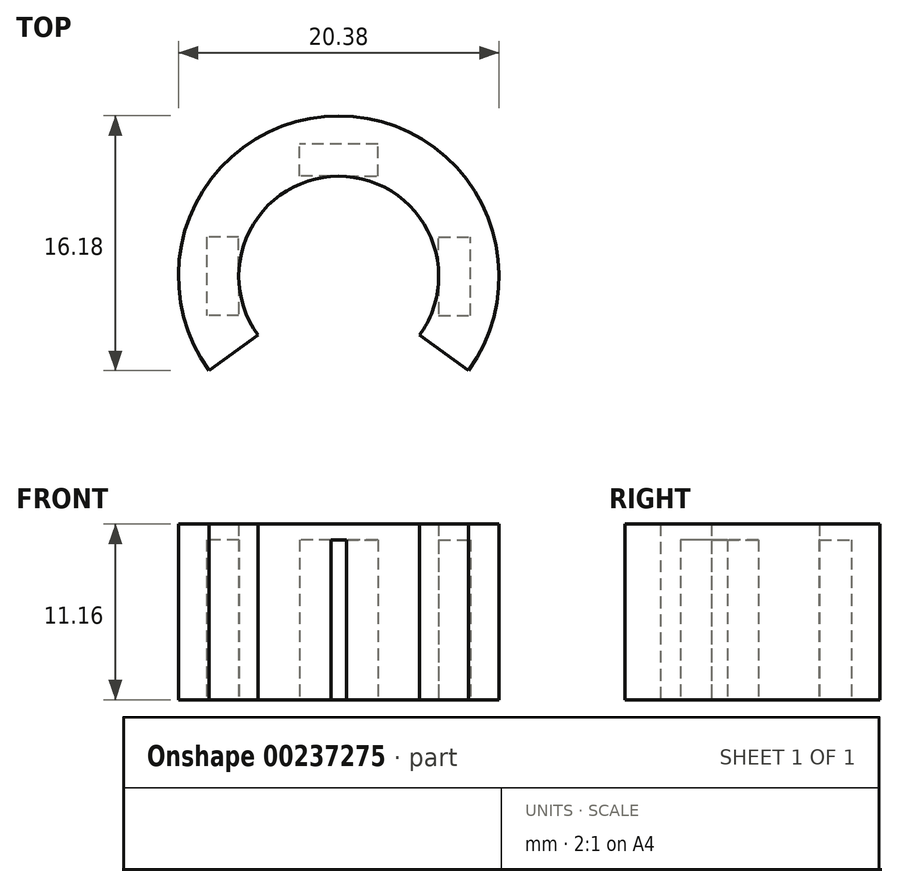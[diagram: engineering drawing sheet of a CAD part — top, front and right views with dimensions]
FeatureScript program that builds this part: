
annotation { "Feature Type Name" : "Feature", "Feature Type Description" : "" }
export const myFeature = defineFeature(function(context is Context, id is Id, definition is map)
    precondition{}
    {
        {
            var Q0;
            Q0=qCreatedBy(makeId("Top.planeOp"),FACE);
            var sketch = newSketch(context, id + "F0", { "sketchPlane" : qUnion([Q0])});
            skLineSegment(sketch, "E0.0", {"start": v(2.49, 6.35) * mm, "end": v(2.49, 8.38) * mm});
            skLineSegment(sketch, "E1.0", {"start": v(-2.49, 6.35) * mm, "end": v(-2.49, 8.38) * mm});
            skLineSegment(sketch, "E2", {"start": v(0.5, 6.35) * mm, "end": v(2.49, 6.35) * mm});
            skLineSegment(sketch, "E3", {"start": v(-0.5, 6.35) * mm, "end": v(-2.49, 6.35) * mm});
            skLineSegment(sketch, "E4.0", {"start": v(2.49, 8.38) * mm, "end": v(-2.49, 8.38) * mm});
            skLineSegment(sketch, "E5.0", {"start": v(3.99, 6.76) * mm, "end": v(3.99, 9.88) * mm});
            skArc(sketch, "E5.1", {"start": v(-3.99, 6.76) * mm, "mid": v(-5.55, 5.55) * mm, "end": v(-6.76, 3.99) * mm});
            skLineSegment(sketch, "E5.2", {"start": v(-3.99, 6.76) * mm, "end": v(-3.99, 9.88) * mm});
            skLineSegment(sketch, "E5.3", {"start": v(3.99, 9.88) * mm, "end": v(-3.99, 9.88) * mm});
            skArc(sketch, "E6.converted", {"start": v(-0.5, 6.33) * mm, "mid": v(-4.5, 4.5) * mm, "end": v(-6.33, 0.5) * mm});
            skPoint(sketch, "E7.orphan", {"position": v(-2.49, 5.84) * mm});
            skPoint(sketch, "E8.orphan", {"position": v(2.49, 5.84) * mm});
            skArc(sketch, "E9", {"start": v(-0.5, 6.35) * mm, "mid": v(-0.5, 6.34) * mm, "end": v(-0.5, 6.33) * mm});
            skArc(sketch, "E10.trimOffspring", {"start": v(0.5, 6.33) * mm, "mid": v(0.5, 6.34) * mm, "end": v(0.5, 6.35) * mm});
            skLineSegment(sketch, "E11.1.0", {"start": v(-9.88, 3.99) * mm, "end": v(-9.88, -3.99) * mm});
            skLineSegment(sketch, "E11.1.1", {"start": v(-6.76, -3.99) * mm, "end": v(-9.88, -3.99) * mm});
            skLineSegment(sketch, "E11.1.2", {"start": v(-6.76, 3.99) * mm, "end": v(-9.88, 3.99) * mm});
            skLineSegment(sketch, "E11.1.3", {"start": v(-8.38, 2.49) * mm, "end": v(-8.38, -2.49) * mm});
            skLineSegment(sketch, "E11.1.4", {"start": v(-6.35, -2.49) * mm, "end": v(-8.38, -2.49) * mm});
            skLineSegment(sketch, "E11.1.5", {"start": v(-6.35, 2.49) * mm, "end": v(-8.38, 2.49) * mm});
            skLineSegment(sketch, "E11.1.6", {"start": v(-6.35, 0.5) * mm, "end": v(-6.35, 2.49) * mm});
            skLineSegment(sketch, "E11.1.7", {"start": v(-6.35, -0.5) * mm, "end": v(-6.35, -2.49) * mm});
            skArc(sketch, "E11.1.9", {"start": v(-6.35, -0.5) * mm, "mid": v(-6.34, -0.5) * mm, "end": v(-6.33, -0.5) * mm});
            skArc(sketch, "E11.1.10", {"start": v(-6.33, 0.5) * mm, "mid": v(-6.34, 0.5) * mm, "end": v(-6.35, 0.5) * mm});
            skLineSegment(sketch, "E12.2.3.0", {"start": v(9.88, -3.99) * mm, "end": v(9.88, 3.99) * mm});
            skLineSegment(sketch, "E12.3.3.0", {"start": v(6.76, 3.99) * mm, "end": v(9.88, 3.99) * mm});
            skLineSegment(sketch, "E12.6.3.0", {"start": v(6.76, -3.99) * mm, "end": v(9.88, -3.99) * mm});
            skLineSegment(sketch, "E12.9.3.0", {"start": v(8.38, -2.49) * mm, "end": v(8.38, 2.49) * mm});
            skLineSegment(sketch, "E12.12.3.0", {"start": v(6.35, 2.49) * mm, "end": v(8.38, 2.49) * mm});
            skLineSegment(sketch, "E12.15.3.0", {"start": v(6.35, -2.49) * mm, "end": v(8.38, -2.49) * mm});
            skLineSegment(sketch, "E12.18.3.0", {"start": v(6.35, -0.5) * mm, "end": v(6.35, -2.49) * mm});
            skLineSegment(sketch, "E12.21.3.0", {"start": v(6.35, 0.5) * mm, "end": v(6.35, 2.49) * mm});
            skArc(sketch, "E12.28.3.0", {"start": v(6.35, 0.5) * mm, "mid": v(6.34, 0.5) * mm, "end": v(6.33, 0.5) * mm});
            skArc(sketch, "E12.32.3.0", {"start": v(6.33, -0.5) * mm, "mid": v(6.34, -0.5) * mm, "end": v(6.35, -0.5) * mm});
            skArc(sketch, "E13.trimOffspring", {"start": v(6.33, 0.5) * mm, "mid": v(4.5, 4.5) * mm, "end": v(0.5, 6.33) * mm});
            skArc(sketch, "E14.trimOffspring", {"start": v(-6.33, -0.5) * mm, "mid": v(-5.96, -2.2) * mm, "end": v(-5.14, -3.73) * mm});
            skArc(sketch, "E15.trimOffspring", {"start": v(-6.33, -0.5) * mm, "mid": v(-6.06, -1.91) * mm, "end": v(-5.47, -3.23) * mm});
            skArc(sketch, "E16.trimOffspring", {"start": v(-6.76, -3.99) * mm, "mid": v(-6.56, -4.3) * mm, "end": v(-6.35, -4.62) * mm});
            skArc(sketch, "E17.trimOffspring", {"start": v(6.76, 3.99) * mm, "mid": v(5.55, 5.55) * mm, "end": v(3.99, 6.76) * mm});
            skArc(sketch, "E18.trimOffspring", {"start": v(5.14, -3.73) * mm, "mid": v(5.96, -2.2) * mm, "end": v(6.33, -0.5) * mm});
            skLineSegment(sketch, "E19", {"start": v(-5.14, -3.73) * mm, "end": v(-6.35, -4.62) * mm});
            skLineSegment(sketch, "E20", {"start": v(5.14, -3.73) * mm, "end": v(6.35, -4.62) * mm});
            skArc(sketch, "E21.trimOffspring", {"start": v(6.35, -4.62) * mm, "mid": v(6.56, -4.3) * mm, "end": v(6.76, -3.99) * mm});
            skPoint(sketch, "E22.orphan", {"position": v(-0.5, -6.33) * mm});
            skSolve(sketch);
        }
        {
            var Q0;
            Q0 = qSketchRegion(id + "F0", true);
            extrude(context, id + "F1", {"entities" : qUnion([Q0]), "depth" : 10.16 * mm});
        }
        {
            var Q0;
            Q0=makeQuery(id+"F1.opExtrude","SWEPT_EDGE",EDGE,{"disambiguationData":[OSD([sQuery(id+"F0.wireOp",EDGE,"E5.2"),sQuery(id+"F0.wireOp",EDGE,"E5.3")])]});
            var Q1;
            Q1=makeQuery(id+"F1.opExtrude","SWEPT_EDGE",EDGE,{"disambiguationData":[OSD([sQuery(id+"F0.wireOp",EDGE,"E5.0"),sQuery(id+"F0.wireOp",EDGE,"E5.3")])]});
            var Q2;
            Q2=makeQuery(id+"F1.opExtrude","SWEPT_EDGE",EDGE,{"disambiguationData":[OSD([sQuery(id+"F0.wireOp",EDGE,"E11.1.0"),sQuery(id+"F0.wireOp",EDGE,"E11.1.2")])]});
            var Q3;
            Q3=makeQuery(id+"F1.opExtrude","SWEPT_EDGE",EDGE,{"disambiguationData":[OSD([sQuery(id+"F0.wireOp",EDGE,"E11.1.0"),sQuery(id+"F0.wireOp",EDGE,"E11.1.1")])]});
            var Q4;
            Q4=makeQuery(id+"F1.opExtrude","SWEPT_EDGE",EDGE,{"disambiguationData":[OSD([sQuery(id+"F0.wireOp",EDGE,"E12.2.3.0"),sQuery(id+"F0.wireOp",EDGE,"E12.3.3.0")])]});
            var Q5;
            Q5=makeQuery(id+"F1.opExtrude","SWEPT_EDGE",EDGE,{"disambiguationData":[OSD([sQuery(id+"F0.wireOp",EDGE,"E12.2.3.0"),sQuery(id+"F0.wireOp",EDGE,"E12.6.3.0")])]});
            fillet(context, id + "F2", {"entities" : qUnion([Q0, Q1, Q2, Q3, Q4, Q5]), "radius" : 3 * mm, "tangentPropagation" : true, "allowEdgeOverflow" : false});
        }
        {
            var Q0;
            Q0=makeQuery(id+"F1.opExtrude","CAP_FACE",FACE,{"disambiguationData":[OSD([sQuery(id+"F0.wireOp",EDGE,"E0.0"),sQuery(id+"F0.wireOp",EDGE,"E1.0"),sQuery(id+"F0.wireOp",EDGE,"E2"),sQuery(id+"F0.wireOp",EDGE,"E3"),sQuery(id+"F0.wireOp",EDGE,"E4.0"),sQuery(id+"F0.wireOp",EDGE,"E5.0"),sQuery(id+"F0.wireOp",EDGE,"E5.1"),sQuery(id+"F0.wireOp",EDGE,"E5.2"),sQuery(id+"F0.wireOp",EDGE,"E5.3"),sQuery(id+"F0.wireOp",EDGE,"E9"),sQuery(id+"F0.wireOp",EDGE,"E10.trimOffspring"),sQuery(id+"F0.wireOp",EDGE,"E11.1.0"),sQuery(id+"F0.wireOp",EDGE,"E11.1.1"),sQuery(id+"F0.wireOp",EDGE,"E11.1.2"),sQuery(id+"F0.wireOp",EDGE,"E11.1.3"),sQuery(id+"F0.wireOp",EDGE,"E11.1.4"),sQuery(id+"F0.wireOp",EDGE,"E11.1.5"),sQuery(id+"F0.wireOp",EDGE,"E11.1.6"),sQuery(id+"F0.wireOp",EDGE,"E11.1.7"),sQuery(id+"F0.wireOp",EDGE,"E11.1.9"),sQuery(id+"F0.wireOp",EDGE,"E11.1.10"),sQuery(id+"F0.wireOp",EDGE,"E12.2.3.0"),sQuery(id+"F0.wireOp",EDGE,"E12.3.3.0"),sQuery(id+"F0.wireOp",EDGE,"E12.6.3.0"),sQuery(id+"F0.wireOp",EDGE,"E12.9.3.0"),sQuery(id+"F0.wireOp",EDGE,"E12.12.3.0"),sQuery(id+"F0.wireOp",EDGE,"E12.15.3.0"),sQuery(id+"F0.wireOp",EDGE,"E12.18.3.0"),sQuery(id+"F0.wireOp",EDGE,"E12.21.3.0"),sQuery(id+"F0.wireOp",EDGE,"E12.28.3.0"),sQuery(id+"F0.wireOp",EDGE,"E12.32.3.0"),sQuery(id+"F0.wireOp",EDGE,"E6.converted"),sQuery(id+"F0.wireOp",EDGE,"E13.trimOffspring"),sQuery(id+"F0.wireOp",EDGE,"E14.trimOffspring"),sQuery(id+"F0.wireOp",EDGE,"E15.trimOffspring"),sQuery(id+"F0.wireOp",EDGE,"E16.trimOffspring"),sQuery(id+"F0.wireOp",EDGE,"E17.trimOffspring"),sQuery(id+"F0.wireOp",EDGE,"E18.trimOffspring"),sQuery(id+"F0.wireOp",EDGE,"E19"),sQuery(id+"F0.wireOp",EDGE,"E20"),sQuery(id+"F0.wireOp",EDGE,"E21.trimOffspring")])],"isStart":false});
            var sketch = newSketch(context, id + "F3", { "sketchPlane" : qUnion([Q0])});
            skLineSegment(sketch, "E23.0.0", {"start": v(-6.76, 3.99) * mm, "end": v(-6.88, 3.99) * mm});
            skArc(sketch, "E23.0.1", {"start": v(-6.88, 3.99) * mm, "mid": v(-9, 3.11) * mm, "end": v(-9.88, 0.99) * mm});
            skLineSegment(sketch, "E23.0.2", {"start": v(-9.88, 0.99) * mm, "end": v(-9.88, -0.99) * mm});
            skArc(sketch, "E23.0.3", {"start": v(-9.88, -0.99) * mm, "mid": v(-9, -3.11) * mm, "end": v(-6.88, -3.99) * mm});
            skLineSegment(sketch, "E23.0.4", {"start": v(-6.88, -3.99) * mm, "end": v(-6.76, -3.99) * mm});
            skArc(sketch, "E23.0.5", {"start": v(-6.76, -3.99) * mm, "mid": v(-6.56, -4.3) * mm, "end": v(-6.35, -4.62) * mm});
            skLineSegment(sketch, "E23.0.6", {"start": v(-6.35, -4.62) * mm, "end": v(-5.14, -3.73) * mm});
            skArc(sketch, "E23.0.7", {"start": v(-5.14, -3.73) * mm, "mid": v(-6.11, -1.72) * mm, "end": v(-6.33, 0.5) * mm});
            skArc(sketch, "E23.0.8", {"start": v(-6.33, -0.5) * mm, "mid": v(-6.34, -0.5) * mm, "end": v(-6.35, -0.5) * mm});
            skLineSegment(sketch, "E23.0.9", {"start": v(-6.35, -0.5) * mm, "end": v(-6.35, -2.49) * mm});
            skLineSegment(sketch, "E23.0.10", {"start": v(-6.35, -2.49) * mm, "end": v(-8.38, -2.49) * mm});
            skLineSegment(sketch, "E23.0.11", {"start": v(-8.38, -2.49) * mm, "end": v(-8.38, 2.49) * mm});
            skLineSegment(sketch, "E23.0.12", {"start": v(-8.38, 2.49) * mm, "end": v(-6.35, 2.49) * mm});
            skLineSegment(sketch, "E23.0.13", {"start": v(-6.35, 2.49) * mm, "end": v(-6.35, 0.5) * mm});
            skArc(sketch, "E23.0.14", {"start": v(-6.35, 0.5) * mm, "mid": v(-6.34, 0.5) * mm, "end": v(-6.33, 0.5) * mm});
            skArc(sketch, "E23.0.15", {"start": v(-6.33, 0.5) * mm, "mid": v(-4.5, 4.5) * mm, "end": v(-0.5, 6.33) * mm});
            skArc(sketch, "E23.0.16", {"start": v(-0.5, 6.33) * mm, "mid": v(-0.5, 6.34) * mm, "end": v(-0.5, 6.35) * mm});
            skLineSegment(sketch, "E23.0.17", {"start": v(-0.5, 6.35) * mm, "end": v(-2.49, 6.35) * mm});
            skLineSegment(sketch, "E23.0.18", {"start": v(-2.49, 6.35) * mm, "end": v(-2.49, 8.38) * mm});
            skLineSegment(sketch, "E23.0.19", {"start": v(-2.49, 8.38) * mm, "end": v(2.49, 8.38) * mm});
            skLineSegment(sketch, "E23.0.20", {"start": v(2.49, 8.38) * mm, "end": v(2.49, 6.35) * mm});
            skLineSegment(sketch, "E23.0.21", {"start": v(2.49, 6.35) * mm, "end": v(0.5, 6.35) * mm});
            skArc(sketch, "E23.0.22", {"start": v(0.5, 6.35) * mm, "mid": v(0.5, 6.34) * mm, "end": v(0.5, 6.33) * mm});
            skArc(sketch, "E23.0.23", {"start": v(0, 6.35) * mm, "mid": v(4.5, 4.5) * mm, "end": v(6.35, 0) * mm});
            skArc(sketch, "E23.0.24", {"start": v(6.33, 0.5) * mm, "mid": v(6.34, 0.5) * mm, "end": v(6.35, 0.5) * mm});
            skLineSegment(sketch, "E23.0.25", {"start": v(6.35, 0.5) * mm, "end": v(6.35, 2.49) * mm});
            skLineSegment(sketch, "E23.0.26", {"start": v(6.35, 2.49) * mm, "end": v(8.38, 2.49) * mm});
            skLineSegment(sketch, "E23.0.27", {"start": v(8.38, 2.49) * mm, "end": v(8.38, -2.49) * mm});
            skLineSegment(sketch, "E23.0.28", {"start": v(8.38, -2.49) * mm, "end": v(6.35, -2.49) * mm});
            skLineSegment(sketch, "E23.0.29", {"start": v(6.35, -2.49) * mm, "end": v(6.35, 0) * mm});
            skArc(sketch, "E23.0.30", {"start": v(6.35, -0.5) * mm, "mid": v(6.34, -0.5) * mm, "end": v(6.33, -0.5) * mm});
            skArc(sketch, "E23.0.31", {"start": v(6.33, -0.5) * mm, "mid": v(5.96, -2.2) * mm, "end": v(5.14, -3.73) * mm});
            skLineSegment(sketch, "E23.0.32", {"start": v(5.14, -3.73) * mm, "end": v(6.35, -4.62) * mm});
            skArc(sketch, "E23.0.33", {"start": v(6.35, -4.62) * mm, "mid": v(6.56, -4.3) * mm, "end": v(6.76, -3.99) * mm});
            skLineSegment(sketch, "E23.0.34", {"start": v(6.76, -3.99) * mm, "end": v(6.88, -3.99) * mm});
            skArc(sketch, "E23.0.35", {"start": v(6.88, -3.99) * mm, "mid": v(9, -3.11) * mm, "end": v(9.88, -0.99) * mm});
            skLineSegment(sketch, "E23.0.36", {"start": v(9.88, -0.99) * mm, "end": v(9.88, 0.99) * mm});
            skArc(sketch, "E23.0.37", {"start": v(9.88, 0.99) * mm, "mid": v(9, 3.11) * mm, "end": v(6.88, 3.99) * mm});
            skLineSegment(sketch, "E23.0.38", {"start": v(6.88, 3.99) * mm, "end": v(6.76, 3.99) * mm});
            skArc(sketch, "E23.0.39", {"start": v(6.76, 3.99) * mm, "mid": v(5.55, 5.55) * mm, "end": v(3.99, 6.76) * mm});
            skLineSegment(sketch, "E23.0.40", {"start": v(3.99, 6.76) * mm, "end": v(3.99, 6.88) * mm});
            skArc(sketch, "E23.0.41", {"start": v(3.99, 6.88) * mm, "mid": v(3.11, 9) * mm, "end": v(0.99, 9.88) * mm});
            skLineSegment(sketch, "E23.0.42", {"start": v(0.99, 9.88) * mm, "end": v(-0.99, 9.88) * mm});
            skArc(sketch, "E23.0.43", {"start": v(-0.99, 9.88) * mm, "mid": v(-3.11, 9) * mm, "end": v(-3.99, 6.88) * mm});
            skLineSegment(sketch, "E23.0.44", {"start": v(-3.99, 6.88) * mm, "end": v(-3.99, 6.76) * mm});
            skArc(sketch, "E23.0.45", {"start": v(-3.99, 6.76) * mm, "mid": v(-5.55, 5.55) * mm, "end": v(-6.76, 3.99) * mm});
            skArc(sketch, "E24.0.7", {"start": v(-5.14, -3.73) * mm, "mid": v(-5.96, -2.2) * mm, "end": v(-6.33, -0.5) * mm});
            skArc(sketch, "E24.0.15", {"start": v(-6.33, 0.5) * mm, "mid": v(-4.3, 4.66) * mm, "end": v(0, 6.35) * mm});
            skArc(sketch, "E24.0.23", {"start": v(0.5, 6.33) * mm, "mid": v(4.5, 4.5) * mm, "end": v(6.33, 0.5) * mm});
            skLineSegment(sketch, "E24.0.29", {"start": v(6.35, -2.49) * mm, "end": v(6.35, -0.5) * mm});
            skSolve(sketch);
        }
        {
            var Q0;
            Q0 = qSketchRegion(id + "F3", true);
            extrude(context, id + "F4", {"entities" : qUnion([Q0]), "operationType" : NewBodyOperationType.ADD, "depth" : 1 * mm});
        }
        {
            var Q0;
            Q0=makeQuery(id+"F1.opExtrude","CAP_FACE",FACE,{"disambiguationData":[OSD([sQuery(id+"F0.wireOp",EDGE,"E0.0"),sQuery(id+"F0.wireOp",EDGE,"E1.0"),sQuery(id+"F0.wireOp",EDGE,"E2"),sQuery(id+"F0.wireOp",EDGE,"E3"),sQuery(id+"F0.wireOp",EDGE,"E4.0"),sQuery(id+"F0.wireOp",EDGE,"E5.0"),sQuery(id+"F0.wireOp",EDGE,"E5.1"),sQuery(id+"F0.wireOp",EDGE,"E5.2"),sQuery(id+"F0.wireOp",EDGE,"E5.3"),sQuery(id+"F0.wireOp",EDGE,"E9"),sQuery(id+"F0.wireOp",EDGE,"E10.trimOffspring"),sQuery(id+"F0.wireOp",EDGE,"E11.1.0"),sQuery(id+"F0.wireOp",EDGE,"E11.1.1"),sQuery(id+"F0.wireOp",EDGE,"E11.1.2"),sQuery(id+"F0.wireOp",EDGE,"E11.1.3"),sQuery(id+"F0.wireOp",EDGE,"E11.1.4"),sQuery(id+"F0.wireOp",EDGE,"E11.1.5"),sQuery(id+"F0.wireOp",EDGE,"E11.1.6"),sQuery(id+"F0.wireOp",EDGE,"E11.1.7"),sQuery(id+"F0.wireOp",EDGE,"E11.1.9"),sQuery(id+"F0.wireOp",EDGE,"E11.1.10"),sQuery(id+"F0.wireOp",EDGE,"E12.2.3.0"),sQuery(id+"F0.wireOp",EDGE,"E12.3.3.0"),sQuery(id+"F0.wireOp",EDGE,"E12.6.3.0"),sQuery(id+"F0.wireOp",EDGE,"E12.9.3.0"),sQuery(id+"F0.wireOp",EDGE,"E12.12.3.0"),sQuery(id+"F0.wireOp",EDGE,"E12.15.3.0"),sQuery(id+"F0.wireOp",EDGE,"E12.18.3.0"),sQuery(id+"F0.wireOp",EDGE,"E12.21.3.0"),sQuery(id+"F0.wireOp",EDGE,"E12.28.3.0"),sQuery(id+"F0.wireOp",EDGE,"E12.32.3.0"),sQuery(id+"F0.wireOp",EDGE,"E6.converted"),sQuery(id+"F0.wireOp",EDGE,"E13.trimOffspring"),sQuery(id+"F0.wireOp",EDGE,"E14.trimOffspring"),sQuery(id+"F0.wireOp",EDGE,"E15.trimOffspring"),sQuery(id+"F0.wireOp",EDGE,"E16.trimOffspring"),sQuery(id+"F0.wireOp",EDGE,"E17.trimOffspring"),sQuery(id+"F0.wireOp",EDGE,"E18.trimOffspring"),sQuery(id+"F0.wireOp",EDGE,"E19"),sQuery(id+"F0.wireOp",EDGE,"E20"),sQuery(id+"F0.wireOp",EDGE,"E21.trimOffspring")])],"isStart":true});
            var sketch = newSketch(context, id + "F5", { "sketchPlane" : qUnion([Q0])});
            skArc(sketch, "E25.0", {"start": v(-3.99, -6.76) * mm, "mid": v(-5.55, -5.55) * mm, "end": v(-6.76, -3.99) * mm});
            skArc(sketch, "E26.0", {"start": v(-9.88, -0.99) * mm, "mid": v(-9, -3.11) * mm, "end": v(-6.88, -3.99) * mm});
            skPoint(sketch, "E27.0", {"position": v(-9.88, 0) * mm});
            skLineSegment(sketch, "E28.0", {"start": v(-9.88, -0.99) * mm, "end": v(-9.88, 0.99) * mm});
            skPoint(sketch, "E29.0", {"position": v(-9, 3.11) * mm});
            skArc(sketch, "E30.0", {"start": v(-6.88, 3.99) * mm, "mid": v(-9, 3.11) * mm, "end": v(-9.88, 0.99) * mm});
            skPoint(sketch, "E31.0", {"position": v(-6.82, 3.99) * mm});
            skLineSegment(sketch, "E32.0", {"start": v(-6.76, 3.99) * mm, "end": v(-6.88, 3.99) * mm});
            skArc(sketch, "E33.0", {"start": v(-6.76, 3.99) * mm, "mid": v(-6.56, 4.3) * mm, "end": v(-6.35, 4.62) * mm});
            skLineSegment(sketch, "E34.0", {"start": v(-6.76, -3.99) * mm, "end": v(-6.88, -3.99) * mm});
            skPoint(sketch, "E35.0", {"position": v(-3.99, -6.82) * mm});
            skLineSegment(sketch, "E36.0", {"start": v(-3.99, -6.76) * mm, "end": v(-3.99, -6.88) * mm});
            skArc(sketch, "E37.0", {"start": v(-3.99, -6.88) * mm, "mid": v(-3.11, -9) * mm, "end": v(-0.99, -9.88) * mm});
            skLineSegment(sketch, "E38.0", {"start": v(0.99, -9.88) * mm, "end": v(-0.99, -9.88) * mm});
            skArc(sketch, "E39.0", {"start": v(0.99, -9.88) * mm, "mid": v(3.11, -9) * mm, "end": v(3.99, -6.88) * mm});
            skLineSegment(sketch, "E40.0", {"start": v(3.99, -6.76) * mm, "end": v(3.99, -6.88) * mm});
            skArc(sketch, "E41.0", {"start": v(6.76, -3.99) * mm, "mid": v(5.55, -5.55) * mm, "end": v(3.99, -6.76) * mm});
            skLineSegment(sketch, "E42.0", {"start": v(6.76, -3.99) * mm, "end": v(6.88, -3.99) * mm});
            skArc(sketch, "E43.0", {"start": v(6.88, -3.99) * mm, "mid": v(9, -3.11) * mm, "end": v(9.88, -0.99) * mm});
            skLineSegment(sketch, "E44.0", {"start": v(9.88, 0.99) * mm, "end": v(9.88, -0.99) * mm});
            skArc(sketch, "E45.0", {"start": v(9.88, 0.99) * mm, "mid": v(9, 3.11) * mm, "end": v(6.88, 3.99) * mm});
            skLineSegment(sketch, "E46.0", {"start": v(6.76, 3.99) * mm, "end": v(6.88, 3.99) * mm});
            skArc(sketch, "E47.0", {"start": v(6.35, 4.62) * mm, "mid": v(6.56, 4.3) * mm, "end": v(6.76, 3.99) * mm});
            skArc(sketch, "E48", {"start": v(-8.03, 5.84) * mm, "mid": v(0, -9.93) * mm, "end": v(8.03, 5.84) * mm});
            skLineSegment(sketch, "E49", {"start": v(6.35, 4.62) * mm, "end": v(8.03, 5.84) * mm});
            skLineSegment(sketch, "E50", {"start": v(-6.35, 4.62) * mm, "end": v(-8.03, 5.84) * mm});
            skSolve(sketch);
        }
        {
            var Q0;
            {var subQ1=sQuery(id+"F5.wireOp",EDGE,"E40.0");Q0=makeQuery(id+"F5.imprint","IMPRINT",FACE,{"disambiguationData":[TD([[makeQuery(id+"F5.imprint","IMPRINT",EDGE,{"derivedFrom":subQ1}),1.0]])]});}
            var Q1;
            {var subQ4=sQuery(id+"F5.wireOp",EDGE,"E46.0");Q1=makeQuery(id+"F5.imprint","IMPRINT",FACE,{"disambiguationData":[TD([[makeQuery(id+"F5.imprint","IMPRINT",EDGE,{"derivedFrom":subQ4}),1.0]])]});}
            var Q2;
            {var subQ4=sQuery(id+"F5.wireOp",EDGE,"E32.0");Q2=makeQuery(id+"F5.imprint","IMPRINT",FACE,{"disambiguationData":[TD([[makeQuery(id+"F5.imprint","IMPRINT",EDGE,{"derivedFrom":subQ4}),-1.0]])]});}
            var Q3;
            Q3=makeQuery(id+"F5.imprint","IMPRINT",FACE,{"disambiguationData":[TD([[makeQuery(id+"F5.imprint","IMPRINT",EDGE,{"derivedFrom":sQuery(id+"F5.wireOp",EDGE,"E25.0")}),1.0]])]});
            var Q4;
            Q4=makeQuery(id+"F4.opExtrude","CAP_VERTEX",VERTEX,{"disambiguationData":[OSD([sQuery(id+"F3.wireOp",EDGE,"E23.0.1"),sQuery(id+"F3.wireOp",EDGE,"E23.0.2")])],"isStart":false});
            extrude(context, id + "F6", {"entities" : qUnion([Q0, Q1, Q2, Q3]), "operationType" : NewBodyOperationType.ADD, "endBound" : BoundingType.UP_TO_VERTEX, "oppositeDirection" : true, "endBoundEntityVertex" : qUnion([Q4]), "depth" : 25.4 * mm});
        }
        {
            var Q0;
            {var subQ0=sQuery(id+"F5.wireOp",EDGE,"E48");Q0=makeQuery(id+"F6.boolean.opBoolean","MERGE",FACE,{"derivedFrom":[makeQuery(id+"F1.opExtrude","CAP_FACE",FACE,{"disambiguationData":[OSD([sQuery(id+"F0.wireOp",EDGE,"E0.0"),sQuery(id+"F0.wireOp",EDGE,"E1.0"),sQuery(id+"F0.wireOp",EDGE,"E2"),sQuery(id+"F0.wireOp",EDGE,"E3"),sQuery(id+"F0.wireOp",EDGE,"E4.0"),sQuery(id+"F0.wireOp",EDGE,"E5.0"),sQuery(id+"F0.wireOp",EDGE,"E5.1"),sQuery(id+"F0.wireOp",EDGE,"E5.2"),sQuery(id+"F0.wireOp",EDGE,"E5.3"),sQuery(id+"F0.wireOp",EDGE,"E9"),sQuery(id+"F0.wireOp",EDGE,"E10.trimOffspring"),sQuery(id+"F0.wireOp",EDGE,"E11.1.0"),sQuery(id+"F0.wireOp",EDGE,"E11.1.1"),sQuery(id+"F0.wireOp",EDGE,"E11.1.2"),sQuery(id+"F0.wireOp",EDGE,"E11.1.3"),sQuery(id+"F0.wireOp",EDGE,"E11.1.4"),sQuery(id+"F0.wireOp",EDGE,"E11.1.5"),sQuery(id+"F0.wireOp",EDGE,"E11.1.6"),sQuery(id+"F0.wireOp",EDGE,"E11.1.7"),sQuery(id+"F0.wireOp",EDGE,"E11.1.9"),sQuery(id+"F0.wireOp",EDGE,"E11.1.10"),sQuery(id+"F0.wireOp",EDGE,"E12.2.3.0"),sQuery(id+"F0.wireOp",EDGE,"E12.3.3.0"),sQuery(id+"F0.wireOp",EDGE,"E12.6.3.0"),sQuery(id+"F0.wireOp",EDGE,"E12.9.3.0"),sQuery(id+"F0.wireOp",EDGE,"E12.12.3.0"),sQuery(id+"F0.wireOp",EDGE,"E12.15.3.0"),sQuery(id+"F0.wireOp",EDGE,"E12.18.3.0"),sQuery(id+"F0.wireOp",EDGE,"E12.21.3.0"),sQuery(id+"F0.wireOp",EDGE,"E12.28.3.0"),sQuery(id+"F0.wireOp",EDGE,"E12.32.3.0"),sQuery(id+"F0.wireOp",EDGE,"E6.converted"),sQuery(id+"F0.wireOp",EDGE,"E13.trimOffspring"),sQuery(id+"F0.wireOp",EDGE,"E14.trimOffspring"),sQuery(id+"F0.wireOp",EDGE,"E15.trimOffspring"),sQuery(id+"F0.wireOp",EDGE,"E16.trimOffspring"),sQuery(id+"F0.wireOp",EDGE,"E17.trimOffspring"),sQuery(id+"F0.wireOp",EDGE,"E18.trimOffspring"),sQuery(id+"F0.wireOp",EDGE,"E19"),sQuery(id+"F0.wireOp",EDGE,"E20"),sQuery(id+"F0.wireOp",EDGE,"E21.trimOffspring")])],"isStart":true}),makeQuery(id+"F6.opExtrude","CAP_FACE",FACE,{"disambiguationData":[OSD([sQuery(id+"F5.wireOp",EDGE,"E25.0"),sQuery(id+"F5.wireOp",EDGE,"E26.0"),sQuery(id+"F5.wireOp",EDGE,"E34.0"),sQuery(id+"F5.wireOp",EDGE,"E36.0"),sQuery(id+"F5.wireOp",EDGE,"E37.0"),subQ0])],"isStart":true}),makeQuery(id+"F6.opExtrude","CAP_FACE",FACE,{"disambiguationData":[OSD([sQuery(id+"F5.wireOp",EDGE,"E30.0"),sQuery(id+"F5.wireOp",EDGE,"E32.0"),sQuery(id+"F5.wireOp",EDGE,"E33.0"),subQ0,sQuery(id+"F5.wireOp",EDGE,"E50")])],"isStart":true}),makeQuery(id+"F6.opExtrude","CAP_FACE",FACE,{"disambiguationData":[OSD([sQuery(id+"F5.wireOp",EDGE,"E39.0"),sQuery(id+"F5.wireOp",EDGE,"E40.0"),sQuery(id+"F5.wireOp",EDGE,"E41.0"),sQuery(id+"F5.wireOp",EDGE,"E42.0"),sQuery(id+"F5.wireOp",EDGE,"E43.0"),subQ0])],"isStart":true}),makeQuery(id+"F6.opExtrude","CAP_FACE",FACE,{"disambiguationData":[OSD([sQuery(id+"F5.wireOp",EDGE,"E45.0"),sQuery(id+"F5.wireOp",EDGE,"E46.0"),sQuery(id+"F5.wireOp",EDGE,"E47.0"),subQ0,sQuery(id+"F5.wireOp",EDGE,"E49")])],"isStart":true})]});}
            var sketch = newSketch(context, id + "F7", { "sketchPlane" : qUnion([Q0])});
            skArc(sketch, "E51", {"start": v(-8.24, 5.99) * mm, "mid": v(0, -10.19) * mm, "end": v(8.24, 5.99) * mm});
            skArc(sketch, "E52", {"start": v(-7.83, 5.69) * mm, "mid": v(0, -9.68) * mm, "end": v(7.83, 5.69) * mm});
            skLineSegment(sketch, "E53", {"start": v(7.83, 5.69) * mm, "end": v(8.24, 5.99) * mm});
            skLineSegment(sketch, "E54", {"start": v(-7.83, 5.69) * mm, "end": v(-8.24, 5.99) * mm});
            skSolve(sketch);
        }
        {
            var Q0;
            Q0 = qSketchRegion(id + "F7", true);
            var Q1;
            {var subQ0=sQuery(id+"F5.wireOp",EDGE,"E48");var subQ1=dummyQuery(id+"F6.vertexPlane.planeOp",FACE);Q1=makeQuery(id+"F6.boolean.opBoolean","MERGE",FACE,{"derivedFrom":[makeQuery(id+"F4.opExtrude","CAP_FACE",FACE,{"disambiguationData":[OSD([sQuery(id+"F3.wireOp",EDGE,"E23.0.7"),sQuery(id+"F3.wireOp",EDGE,"E23.0.23"),sQuery(id+"F3.wireOp",EDGE,"E23.0.29"),sQuery(id+"F3.wireOp",EDGE,"E23.0.0"),sQuery(id+"F3.wireOp",EDGE,"E23.0.1"),sQuery(id+"F3.wireOp",EDGE,"E23.0.2"),sQuery(id+"F3.wireOp",EDGE,"E23.0.3"),sQuery(id+"F3.wireOp",EDGE,"E23.0.4"),sQuery(id+"F3.wireOp",EDGE,"E23.0.5"),sQuery(id+"F3.wireOp",EDGE,"E23.0.6"),sQuery(id+"F3.wireOp",EDGE,"E24.0.7"),sQuery(id+"F3.wireOp",EDGE,"E24.0.15"),sQuery(id+"F3.wireOp",EDGE,"E24.0.23"),sQuery(id+"F3.wireOp",EDGE,"E23.0.30"),sQuery(id+"F3.wireOp",EDGE,"E23.0.31"),sQuery(id+"F3.wireOp",EDGE,"E23.0.32"),sQuery(id+"F3.wireOp",EDGE,"E23.0.33"),sQuery(id+"F3.wireOp",EDGE,"E23.0.34"),sQuery(id+"F3.wireOp",EDGE,"E23.0.35"),sQuery(id+"F3.wireOp",EDGE,"E23.0.36"),sQuery(id+"F3.wireOp",EDGE,"E23.0.37"),sQuery(id+"F3.wireOp",EDGE,"E23.0.38"),sQuery(id+"F3.wireOp",EDGE,"E23.0.39"),sQuery(id+"F3.wireOp",EDGE,"E23.0.40"),sQuery(id+"F3.wireOp",EDGE,"E23.0.41"),sQuery(id+"F3.wireOp",EDGE,"E23.0.42"),sQuery(id+"F3.wireOp",EDGE,"E23.0.43"),sQuery(id+"F3.wireOp",EDGE,"E23.0.44"),sQuery(id+"F3.wireOp",EDGE,"E23.0.45")])],"isStart":false}),makeQuery(id+"F6.opExtrude","CAP_FACE",FACE,{"disambiguationData":[OSD([subQ1]),ownerDisambiguation([makeQuery(id+"F6.opExtrude","SWEPT_BODY",BODY,{"disambiguationData":[OSD([sQuery(id+"F5.wireOp",EDGE,"E25.0"),sQuery(id+"F5.wireOp",EDGE,"E26.0"),sQuery(id+"F5.wireOp",EDGE,"E34.0"),sQuery(id+"F5.wireOp",EDGE,"E36.0"),sQuery(id+"F5.wireOp",EDGE,"E37.0"),subQ0])]})])],"isStart":false}),makeQuery(id+"F6.opExtrude","CAP_FACE",FACE,{"disambiguationData":[OSD([subQ1]),ownerDisambiguation([makeQuery(id+"F6.opExtrude","SWEPT_BODY",BODY,{"disambiguationData":[OSD([sQuery(id+"F5.wireOp",EDGE,"E30.0"),sQuery(id+"F5.wireOp",EDGE,"E32.0"),sQuery(id+"F5.wireOp",EDGE,"E33.0"),subQ0,sQuery(id+"F5.wireOp",EDGE,"E50")])]})])],"isStart":false}),makeQuery(id+"F6.opExtrude","CAP_FACE",FACE,{"disambiguationData":[OSD([subQ1]),ownerDisambiguation([makeQuery(id+"F6.opExtrude","SWEPT_BODY",BODY,{"disambiguationData":[OSD([sQuery(id+"F5.wireOp",EDGE,"E39.0"),sQuery(id+"F5.wireOp",EDGE,"E40.0"),sQuery(id+"F5.wireOp",EDGE,"E41.0"),sQuery(id+"F5.wireOp",EDGE,"E42.0"),sQuery(id+"F5.wireOp",EDGE,"E43.0"),subQ0])]})])],"isStart":false}),makeQuery(id+"F6.opExtrude","CAP_FACE",FACE,{"disambiguationData":[OSD([subQ1]),ownerDisambiguation([makeQuery(id+"F6.opExtrude","SWEPT_BODY",BODY,{"disambiguationData":[OSD([sQuery(id+"F5.wireOp",EDGE,"E45.0"),sQuery(id+"F5.wireOp",EDGE,"E46.0"),sQuery(id+"F5.wireOp",EDGE,"E47.0"),subQ0,sQuery(id+"F5.wireOp",EDGE,"E49")])]})])],"isStart":false})]});}
            extrude(context, id + "F8", {"entities" : qUnion([Q0]), "operationType" : NewBodyOperationType.ADD, "endBound" : BoundingType.UP_TO_SURFACE, "oppositeDirection" : true, "endBoundEntityFace" : qUnion([Q1]), "depth" : 25.4 * mm});
        }
    });
